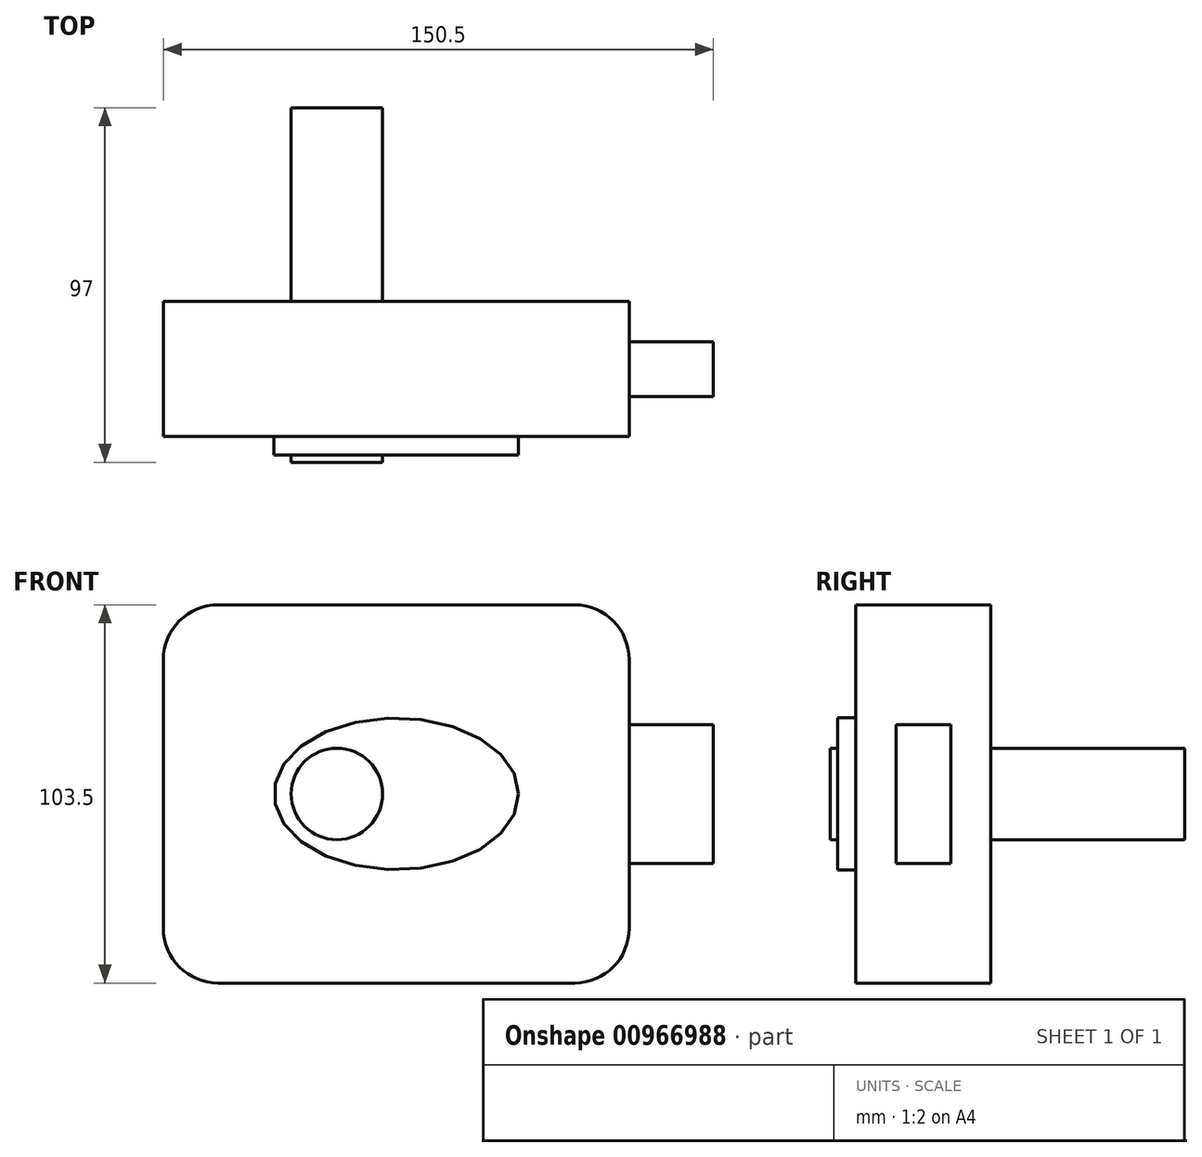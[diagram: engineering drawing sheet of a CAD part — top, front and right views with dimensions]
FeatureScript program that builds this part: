
annotation { "Feature Type Name" : "Feature", "Feature Type Description" : "" }
export const myFeature = defineFeature(function(context is Context, id is Id, definition is map)
    precondition{}
    {
        {
            var Q0;
            Q0=qCreatedBy(makeId("Front.planeOp"),FACE);
            var sketch = newSketch(context, id + "F0", { "sketchPlane" : qUnion([Q0])});
            skLineSegment(sketch, "E0.bottom", {"start": v(0, 0) * mm, "end": v(127.5, 0) * mm});
            skLineSegment(sketch, "E0.top", {"start": v(0, 103.5) * mm, "end": v(127.5, 103.5) * mm});
            skLineSegment(sketch, "E0.left", {"start": v(0, 0) * mm, "end": v(0, 103.5) * mm});
            skLineSegment(sketch, "E0.right", {"start": v(127.5, 0) * mm, "end": v(127.5, 103.5) * mm});
            skSolve(sketch);
        }
        {
            var Q0;
            Q0 = qSketchRegion(id + "F0", true);
            extrude(context, id + "F1", {"entities" : qUnion([Q0]), "depth" : 37 * mm, "offsetDistance" : 25 * mm});
        }
        {
            var Q0;
            Q0=makeQuery(id+"F1.opExtrude","SWEPT_EDGE",EDGE,{"disambiguationData":[OSD([sQuery(id+"F0.wireOp",EDGE,"E0.top"),sQuery(id+"F0.wireOp",EDGE,"E0.right")])]});
            var Q1;
            Q1=makeQuery(id+"F1.opExtrude","SWEPT_EDGE",EDGE,{"disambiguationData":[OSD([sQuery(id+"F0.wireOp",EDGE,"E0.top"),sQuery(id+"F0.wireOp",EDGE,"E0.left")])]});
            var Q2;
            Q2=makeQuery(id+"F1.opExtrude","SWEPT_EDGE",EDGE,{"disambiguationData":[OSD([sQuery(id+"F0.wireOp",EDGE,"E0.bottom"),sQuery(id+"F0.wireOp",EDGE,"E0.right")])]});
            var Q3;
            Q3=makeQuery(id+"F1.opExtrude","SWEPT_EDGE",EDGE,{"disambiguationData":[OSD([sQuery(id+"F0.wireOp",EDGE,"E0.bottom"),sQuery(id+"F0.wireOp",EDGE,"E0.left")])]});
            fillet(context, id + "F2", {"entities" : qUnion([Q0, Q1, Q2, Q3]), "radius" : 15 * mm, "tangentPropagation" : true, "allowEdgeOverflow" : false});
        }
        {
            var Q0;
            Q0=makeQuery(id+"F1.opExtrude","SWEPT_FACE",FACE,{"disambiguationData":[OSD([sQuery(id+"F0.wireOp",EDGE,"E0.right")])]});
            var sketch = newSketch(context, id + "F3", { "sketchPlane" : qUnion([Q0])});
            skLineSegment(sketch, "E1.bottom", {"start": v(-11, 32.75) * mm, "end": v(-26, 32.75) * mm});
            skLineSegment(sketch, "E1.top", {"start": v(-11, 70.75) * mm, "end": v(-26, 70.75) * mm});
            skLineSegment(sketch, "E1.left", {"start": v(-11, 32.75) * mm, "end": v(-11, 70.75) * mm});
            skLineSegment(sketch, "E1.right", {"start": v(-26, 32.75) * mm, "end": v(-26, 70.75) * mm});
            skPoint(sketch, "E1.middle", {"position": v(-18.5, 51.75) * mm});
            skPoint(sketch, "E1.middle.positionSnap0", {"position": v(-37, 51.75) * mm});
            skPoint(sketch, "E1.middle.positionSnap1", {"position": v(-18.5, 88.5) * mm});
            skPoint(sketch, "E1.centerSnap0", {"position": v(-37, 51.75) * mm});
            skPoint(sketch, "E1.centerSnap1", {"position": v(-18.5, 88.5) * mm});
            skSolve(sketch);
        }
        {
            var Q0;
            Q0 = qSketchRegion(id + "F3", true);
            extrude(context, id + "F4", {"entities" : qUnion([Q0]), "operationType" : NewBodyOperationType.ADD, "depth" : 23 * mm, "offsetDistance" : 25 * mm});
        }
        {
            var Q0;
            Q0=makeQuery(id+"F1.opExtrude","CAP_FACE",FACE,{"disambiguationData":[OSD([sQuery(id+"F0.wireOp",EDGE,"E0.bottom"),sQuery(id+"F0.wireOp",EDGE,"E0.top"),sQuery(id+"F0.wireOp",EDGE,"E0.left"),sQuery(id+"F0.wireOp",EDGE,"E0.right")])],"isStart":false});
            var sketch = newSketch(context, id + "F5", { "sketchPlane" : qUnion([Q0])});
            skLineSegment(sketch, "E2", {"start": v(63.75, 103.5) * mm, "end": v(63.75, 0) * mm, "construction": true});
            skLineSegment(sketch, "E3", {"start": v(0, 51.75) * mm, "end": v(127.5, 51.75) * mm, "construction": true});
            skEllipse(sketch, "E4", {"center": v(63.75, 51.75) * mm, "majorRadius": 33.46 * mm, "minorRadius": 20.79 * mm, "majorAxis": v(1, 0)});
            skSolve(sketch);
        }
        {
            var Q0;
            Q0 = qSketchRegion(id + "F5", true);
            extrude(context, id + "F6", {"entities" : qUnion([Q0]), "operationType" : NewBodyOperationType.ADD, "depth" : 5 * mm, "offsetDistance" : 25 * mm});
        }
        {
            var Q0;
            Q0=makeQuery(id+"F6.opExtrude","CAP_FACE",FACE,{"disambiguationData":[OSD([sQuery(id+"F5.wireOp",EDGE,"E4")])],"isStart":false});
            var sketch = newSketch(context, id + "F7", { "sketchPlane" : qUnion([Q0])});
            skCircle(sketch, "E5", {"center": v(47.5, 51.75) * mm, "radius": 12.5 * mm});
            skSolve(sketch);
        }
        {
            var Q0;
            Q0 = qSketchRegion(id + "F7", true);
            extrude(context, id + "F8", {"entities" : qUnion([Q0]), "operationType" : NewBodyOperationType.ADD, "oppositeDirection" : true, "depth" : 95 * mm, "offsetDistance" : 25 * mm});
        }
        {
            var Q0;
            Q0 = qSketchRegion(id + "F7", true);
            extrude(context, id + "F9", {"entities" : qUnion([Q0]), "operationType" : NewBodyOperationType.ADD, "depth" : 2 * mm, "offsetDistance" : 25 * mm});
        }
    });
